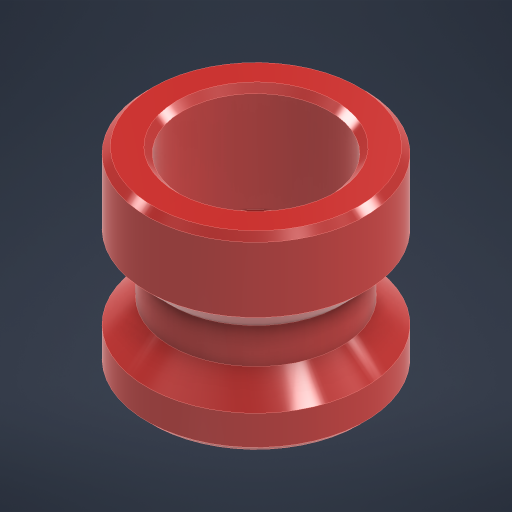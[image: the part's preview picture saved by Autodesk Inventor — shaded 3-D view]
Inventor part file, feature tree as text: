
AUTODESK INVENTOR PART (.ipt)
format: ipt  version: 2024.1 (Build 281209000, 209)  size: 261,632 bytes
history: native  units: mm
features: chamfer x2, revolve x1, sketch x1
ambient origin geometry x8: Origin, YZ Plane, XZ Plane, XY Plane, X Axis, Y Axis, Z Axis, Center Point
bodies: Solid1 (feature_tree)
feature tree (4):
  revolve  "Revolution1"  [1 undecoded]
  chamfer  "Chamfer1"  Distance=3.0mm
  chamfer  "Chamfer2"  Distance=3.5mm
  sketch  "Sketch1"  dims[d0=1.6mm d1=8.0mm d2=3.0mm d3=3.5mm d4=1.5mm d5=4.0mm d6=1.0mm d7=1.5mm d8=360.0deg d9=1.0mm d10=2.0mm d11=45.0deg d12=0.25mm d13=2.0mm d14=45.0deg]
note: 1 required parameter value undecoded (feature->parameter linkage not recoverable at this tier; creation-order binding heuristic only, values carry confidence <= 0.55)
